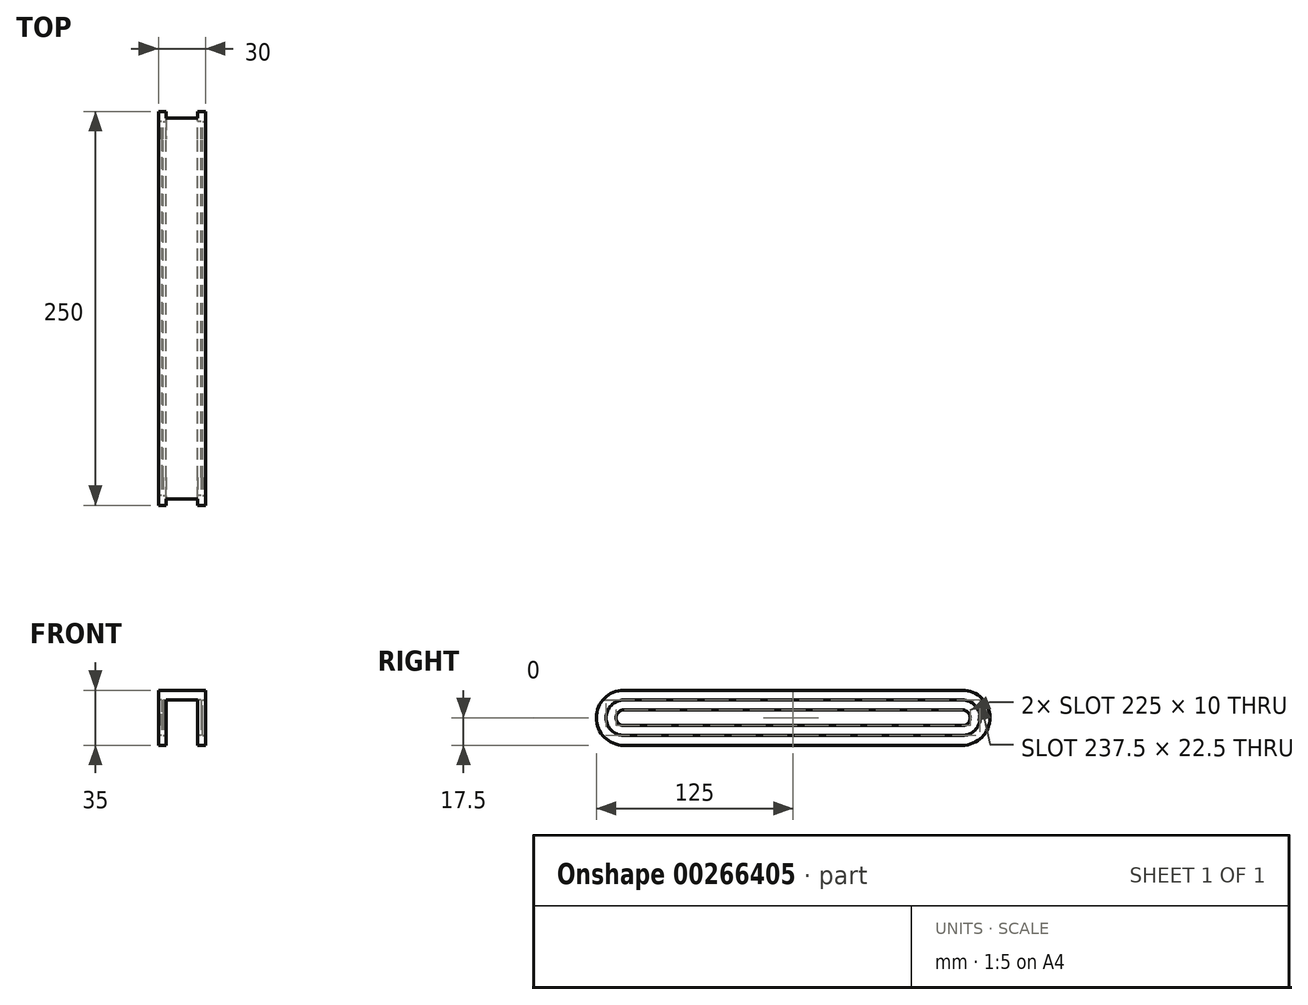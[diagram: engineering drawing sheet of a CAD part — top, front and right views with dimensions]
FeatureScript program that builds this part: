
annotation { "Feature Type Name" : "Feature", "Feature Type Description" : "" }
export const myFeature = defineFeature(function(context is Context, id is Id, definition is map)
    precondition{}
    {
        {
            var Q0;
            Q0=qCreatedBy(makeId("Front.planeOp"),FACE);
            var sketch = newSketch(context, id + "F0", { "sketchPlane" : qUnion([Q0])});
            skLineSegment(sketch, "E0.top", {"start": v(15, 17.5) * mm, "end": v(-15, 17.5) * mm});
            skLineSegment(sketch, "E0.left", {"start": v(15, -17.5) * mm, "end": v(15, 17.5) * mm});
            skLineSegment(sketch, "E0.right", {"start": v(-15, -17.5) * mm, "end": v(-15, 17.5) * mm});
            skPoint(sketch, "E0.middle", {"position": v(0, 0) * mm});
            skLineSegment(sketch, "E1", {"start": v(-15, -17.5) * mm, "end": v(-10, -17.5) * mm});
            skLineSegment(sketch, "E2", {"start": v(-10, -17.5) * mm, "end": v(-10, 11.25) * mm});
            skLineSegment(sketch, "E3", {"start": v(-10, 11.25) * mm, "end": v(10, 11.25) * mm});
            skLineSegment(sketch, "E4", {"start": v(10, 11.25) * mm, "end": v(10, -17.5) * mm});
            skLineSegment(sketch, "E5", {"start": v(10, -17.5) * mm, "end": v(15, -17.5) * mm});
            skSolve(sketch);
        }
        {
            var Q0;
            Q0=makeQuery(id+"F0.imprint","IMPRINT",FACE,{"disambiguationData":[TD([[makeQuery(id+"F0.imprint","IMPRINT",EDGE,{"derivedFrom":sQuery(id+"F0.wireOp",EDGE,"E0.top")}),1.0]])]});
            extrude(context, id + "F1", {"entities" : qUnion([Q0]), "depth" : 125 * mm, "hasSecondDirection" : true, "secondDirectionOppositeDirection" : true, "secondDirectionDepth" : 125 * mm});
        }
        {
            var Q0;
            Q0=makeQuery(id+"F1.opExtrude","SWEPT_FACE",FACE,{"disambiguationData":[OSD([sQuery(id+"F0.wireOp",EDGE,"E4")])]});
            var sketch = newSketch(context, id + "F2", { "sketchPlane" : qUnion([Q0])});
            skLineSegment(sketch, "E6", {"start": v(107.5, -11.25) * mm, "end": v(-107.5, -11.25) * mm});
            skLineSegment(sketch, "E7", {"start": v(107.5, 11.25) * mm, "end": v(-107.5, 11.25) * mm});
            skLineSegment(sketch, "E8", {"start": v(107.5, -5) * mm, "end": v(-107.5, -5) * mm});
            skLineSegment(sketch, "E9", {"start": v(107.5, 5) * mm, "end": v(-107.5, 5) * mm});
            skArc(sketch, "E10", {"start": v(-107.5, 5) * mm, "mid": v(-112.5, 0) * mm, "end": v(-107.5, -5) * mm});
            skArc(sketch, "E11", {"start": v(-107.5, 11.25) * mm, "mid": v(-118.75, 0) * mm, "end": v(-107.5, -11.25) * mm});
            skArc(sketch, "E12", {"start": v(107.5, -5) * mm, "mid": v(112.5, 0) * mm, "end": v(107.5, 5) * mm});
            skArc(sketch, "E13", {"start": v(107.5, -11.25) * mm, "mid": v(118.75, 0) * mm, "end": v(107.5, 11.25) * mm});
            skSolve(sketch);
        }
        {
            var Q0;
            Q0=makeQuery(id+"F1.opExtrude","SWEPT_FACE",FACE,{"disambiguationData":[OSD([sQuery(id+"F0.wireOp",EDGE,"E0.left")])]});
            var sketch = newSketch(context, id + "F3", { "sketchPlane" : qUnion([Q0])});
            skLineSegment(sketch, "E14", {"start": v(-107.5, -11.25) * mm, "end": v(107.5, -11.25) * mm});
            skLineSegment(sketch, "E15", {"start": v(-107.5, 11.25) * mm, "end": v(107.5, 11.25) * mm});
            skLineSegment(sketch, "E16", {"start": v(-107.5, 5) * mm, "end": v(107.5, 5) * mm});
            skLineSegment(sketch, "E17", {"start": v(-107.5, -5) * mm, "end": v(107.5, -5) * mm});
            skArc(sketch, "E18", {"start": v(-107.5, 5) * mm, "mid": v(-112.5, 0) * mm, "end": v(-107.5, -5) * mm});
            skArc(sketch, "E19", {"start": v(107.5, -5) * mm, "mid": v(112.5, 0) * mm, "end": v(107.5, 5) * mm});
            skArc(sketch, "E20", {"start": v(107.5, -11.25) * mm, "mid": v(118.75, 0) * mm, "end": v(107.5, 11.25) * mm});
            skArc(sketch, "E21", {"start": v(-107.5, 11.25) * mm, "mid": v(-118.75, 0) * mm, "end": v(-107.5, -11.25) * mm});
            skSolve(sketch);
        }
        {
            var Q0;
            Q0=makeQuery(id+"F1.opExtrude","SWEPT_FACE",FACE,{"disambiguationData":[OSD([sQuery(id+"F0.wireOp",EDGE,"E2")])]});
            var sketch = newSketch(context, id + "F4", { "sketchPlane" : qUnion([Q0])});
            skLineSegment(sketch, "E22", {"start": v(-107.5, 11.25) * mm, "end": v(107.5, 11.25) * mm});
            skLineSegment(sketch, "E23", {"start": v(-107.5, -11.25) * mm, "end": v(107.5, -11.25) * mm});
            skLineSegment(sketch, "E24", {"start": v(-107.5, 5) * mm, "end": v(107.5, 5) * mm});
            skLineSegment(sketch, "E25", {"start": v(-107.5, -5) * mm, "end": v(107.5, -5) * mm});
            skPoint(sketch, "E26.start.orphan", {"position": v(125, -3.13) * mm});
            skPoint(sketch, "E27.start.orphan", {"position": v(-125, -3.13) * mm});
            skArc(sketch, "E28", {"start": v(-107.5, 5) * mm, "mid": v(-112.5, 0) * mm, "end": v(-107.5, -5) * mm});
            skArc(sketch, "E29", {"start": v(-107.5, 11.25) * mm, "mid": v(-118.75, 0) * mm, "end": v(-107.5, -11.25) * mm});
            skArc(sketch, "E30", {"start": v(107.5, -5) * mm, "mid": v(112.5, 0) * mm, "end": v(107.5, 5) * mm});
            skArc(sketch, "E31", {"start": v(107.5, -11.25) * mm, "mid": v(118.75, 0) * mm, "end": v(107.5, 11.25) * mm});
            skSolve(sketch);
        }
        {
            var Q0;
            Q0=makeQuery(id+"F1.opExtrude","SWEPT_FACE",FACE,{"disambiguationData":[OSD([sQuery(id+"F0.wireOp",EDGE,"E0.right")])]});
            var sketch = newSketch(context, id + "F5", { "sketchPlane" : qUnion([Q0])});
            skLineSegment(sketch, "E32", {"start": v(-107.5, 11.25) * mm, "end": v(107.5, 11.25) * mm});
            skLineSegment(sketch, "E33", {"start": v(-107.5, -11.25) * mm, "end": v(107.5, -11.25) * mm});
            skLineSegment(sketch, "E34", {"start": v(-107.5, 5) * mm, "end": v(107.5, 5) * mm});
            skLineSegment(sketch, "E35", {"start": v(-107.5, -5) * mm, "end": v(107.5, -5) * mm});
            skArc(sketch, "E36", {"start": v(-107.5, 11.25) * mm, "mid": v(-118.75, 0) * mm, "end": v(-107.5, -11.25) * mm});
            skArc(sketch, "E37", {"start": v(-107.5, 5) * mm, "mid": v(-112.5, 0) * mm, "end": v(-107.5, -5) * mm});
            skArc(sketch, "E38", {"start": v(107.5, -5) * mm, "mid": v(112.5, 0) * mm, "end": v(107.5, 5) * mm});
            skArc(sketch, "E39", {"start": v(107.5, -11.25) * mm, "mid": v(118.75, 0) * mm, "end": v(107.5, 11.25) * mm});
            skSolve(sketch);
        }
        {
            var Q0;
            Q0=makeQuery(id+"F2.imprint","IMPRINT",FACE,{"disambiguationData":[TD([[makeQuery(id+"F2.imprint","IMPRINT",EDGE,{"derivedFrom":sQuery(id+"F2.wireOp",EDGE,"E8")}),-1.0]])]});
            extrude(context, id + "F6", {"entities" : qUnion([Q0]), "operationType" : NewBodyOperationType.REMOVE, "endBound" : BoundingType.THROUGH_ALL, "oppositeDirection" : true, "depth" : 25 * mm});
        }
        {
            var Q0;
            Q0=makeQuery(id+"F4.imprint","IMPRINT",FACE,{"disambiguationData":[TD([[makeQuery(id+"F4.imprint","IMPRINT",EDGE,{"derivedFrom":sQuery(id+"F4.wireOp",EDGE,"E24")}),-1.0]])]});
            extrude(context, id + "F7", {"entities" : qUnion([Q0]), "operationType" : NewBodyOperationType.REMOVE, "endBound" : BoundingType.THROUGH_ALL, "oppositeDirection" : true, "depth" : 25 * mm});
        }
        {
            var Q0;
            Q0=makeQuery(id+"F2.imprint","IMPRINT",FACE,{"disambiguationData":[TD([[makeQuery(id+"F2.imprint","IMPRINT",EDGE,{"derivedFrom":sQuery(id+"F2.wireOp",EDGE,"E6")}),-1.0]])]});
            extrude(context, id + "F8", {"entities" : qUnion([Q0]), "operationType" : NewBodyOperationType.REMOVE, "oppositeDirection" : true, "depth" : 2 * mm});
        }
        {
            var Q0;
            Q0=makeQuery(id+"F3.imprint","IMPRINT",FACE,{"disambiguationData":[TD([[makeQuery(id+"F3.imprint","IMPRINT",EDGE,{"derivedFrom":sQuery(id+"F3.wireOp",EDGE,"E14")}),1.0]])]});
            extrude(context, id + "F9", {"entities" : qUnion([Q0]), "operationType" : NewBodyOperationType.REMOVE, "oppositeDirection" : true, "depth" : 2 * mm});
        }
        {
            var Q0;
            Q0=makeQuery(id+"F5.imprint","IMPRINT",FACE,{"disambiguationData":[TD([[makeQuery(id+"F5.imprint","IMPRINT",EDGE,{"derivedFrom":sQuery(id+"F5.wireOp",EDGE,"E32")}),-1.0]])]});
            extrude(context, id + "F10", {"entities" : qUnion([Q0]), "operationType" : NewBodyOperationType.REMOVE, "oppositeDirection" : true, "depth" : 2 * mm});
        }
        {
            var Q0;
            Q0=makeQuery(id+"F4.imprint","IMPRINT",FACE,{"disambiguationData":[TD([[makeQuery(id+"F4.imprint","IMPRINT",EDGE,{"derivedFrom":sQuery(id+"F4.wireOp",EDGE,"E22")}),-1.0]])]});
            extrude(context, id + "F11", {"entities" : qUnion([Q0]), "operationType" : NewBodyOperationType.REMOVE, "oppositeDirection" : true, "depth" : 2 * mm});
        }
        {
            var Q0;
            Q0=makeQuery(id+"F1.opExtrude","CAP_EDGE",EDGE,{"disambiguationData":[OSD([sQuery(id+"F0.wireOp",EDGE,"E1")])],"isStart":true});
            var Q1;
            Q1=makeQuery(id+"F1.opExtrude","CAP_EDGE",EDGE,{"disambiguationData":[OSD([sQuery(id+"F0.wireOp",EDGE,"E5")])],"isStart":true});
            var Q2;
            Q2=makeQuery(id+"F1.opExtrude","CAP_EDGE",EDGE,{"disambiguationData":[OSD([sQuery(id+"F0.wireOp",EDGE,"E0.top")])],"isStart":true});
            var Q3;
            Q3=makeQuery(id+"F1.opExtrude","CAP_EDGE",EDGE,{"disambiguationData":[OSD([sQuery(id+"F0.wireOp",EDGE,"E0.top")])],"isStart":false});
            var Q4;
            Q4=makeQuery(id+"F1.opExtrude","CAP_EDGE",EDGE,{"disambiguationData":[OSD([sQuery(id+"F0.wireOp",EDGE,"E1")])],"isStart":false});
            var Q5;
            Q5=makeQuery(id+"F1.opExtrude","CAP_EDGE",EDGE,{"disambiguationData":[OSD([sQuery(id+"F0.wireOp",EDGE,"E5")])],"isStart":false});
            fillet(context, id + "F12", {"entities" : qUnion([Q0, Q1, Q2, Q3, Q4, Q5]), "radius" : 17.5 * mm, "tangentPropagation" : true, "allowEdgeOverflow" : false});
        }
    });
